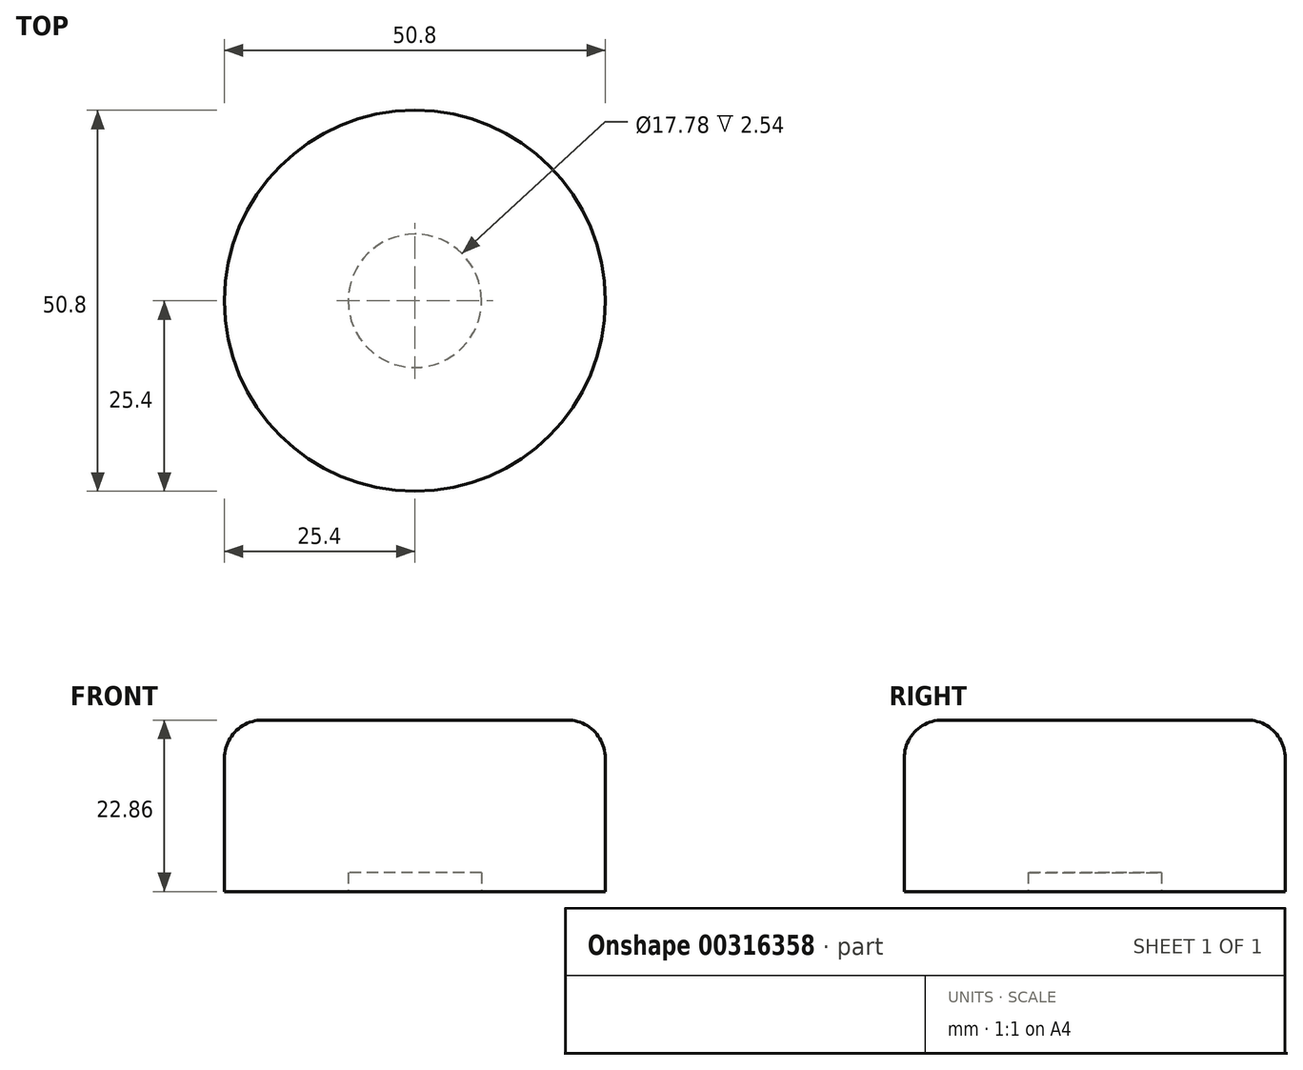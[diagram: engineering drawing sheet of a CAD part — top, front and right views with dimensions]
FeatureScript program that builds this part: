
annotation { "Feature Type Name" : "Feature", "Feature Type Description" : "" }
export const myFeature = defineFeature(function(context is Context, id is Id, definition is map)
    precondition{}
    {
        {
            var Q0;
            Q0=qCreatedBy(makeId("Top.planeOp"),FACE);
            var sketch = newSketch(context, id + "F0", { "sketchPlane" : qUnion([Q0])});
            skCircle(sketch, "E0", {"center": v(0, 0) * mm, "radius": 25.4 * mm});
            skCircle(sketch, "E1", {"center": v(0, 0) * mm, "radius": 8.9 * mm});
            skSolve(sketch);
        }
        {
            var Q0;
            Q0=makeQuery(id+"F0.imprint","IMPRINT",FACE,{"disambiguationData":[TD([[makeQuery(id+"F0.imprint","IMPRINT",EDGE,{"derivedFrom":sQuery(id+"F0.wireOp",EDGE,"E0")}),1.0]])]});
            extrude(context, id + "F1", {"entities" : qUnion([Q0]), "depth" : 2.54 * mm});
        }
        {
            var Q0;
            Q0=makeQuery(id+"F1.opExtrude","CAP_FACE",FACE,{"disambiguationData":[OSD([sQuery(id+"F0.wireOp",EDGE,"E0"),sQuery(id+"F0.wireOp",EDGE,"E1")])],"isStart":false});
            var sketch = newSketch(context, id + "F2", { "sketchPlane" : qUnion([Q0])});
            skCircle(sketch, "E2", {"center": v(0, 0) * mm, "radius": 59.09 * mm});
            skSolve(sketch);
        }
        {
            var Q0;
            Q0=makeQuery(id+"F2.imprint","IMPRINT",FACE,{"disambiguationData":[TD([[makeQuery(id+"F2.imprint","IMPRINT",EDGE,{"derivedFrom":makeQuery(id+"F1.opExtrude","CAP_EDGE",EDGE,{"disambiguationData":[OSD([sQuery(id+"F0.wireOp",EDGE,"E0")])],"isStart":false})}),1.0]])]});
            var Q1;
            Q1=makeQuery(id+"F2.imprint","IMPRINT",FACE,{"disambiguationData":[TD([[makeQuery(id+"F2.imprint","IMPRINT",EDGE,{"derivedFrom":makeQuery(id+"F1.opExtrude","CAP_EDGE",EDGE,{"disambiguationData":[OSD([sQuery(id+"F0.wireOp",EDGE,"E1")])],"isStart":false})}),1.0]])]});
            extrude(context, id + "F3", {"entities" : qUnion([Q0, Q1]), "operationType" : NewBodyOperationType.ADD, "depth" : 20.32 * mm});
        }
        {
            var Q0;
            Q0=makeQuery(id+"F3.opExtrude","CAP_EDGE",EDGE,{"disambiguationData":[OSD([sQuery(id+"F0.wireOp",EDGE,"E0")])],"isStart":false});
            fillet(context, id + "F4", {"entities" : qUnion([Q0]), "radius" : 5.08 * mm, "tangentPropagation" : true, "allowEdgeOverflow" : false});
        }
    });
